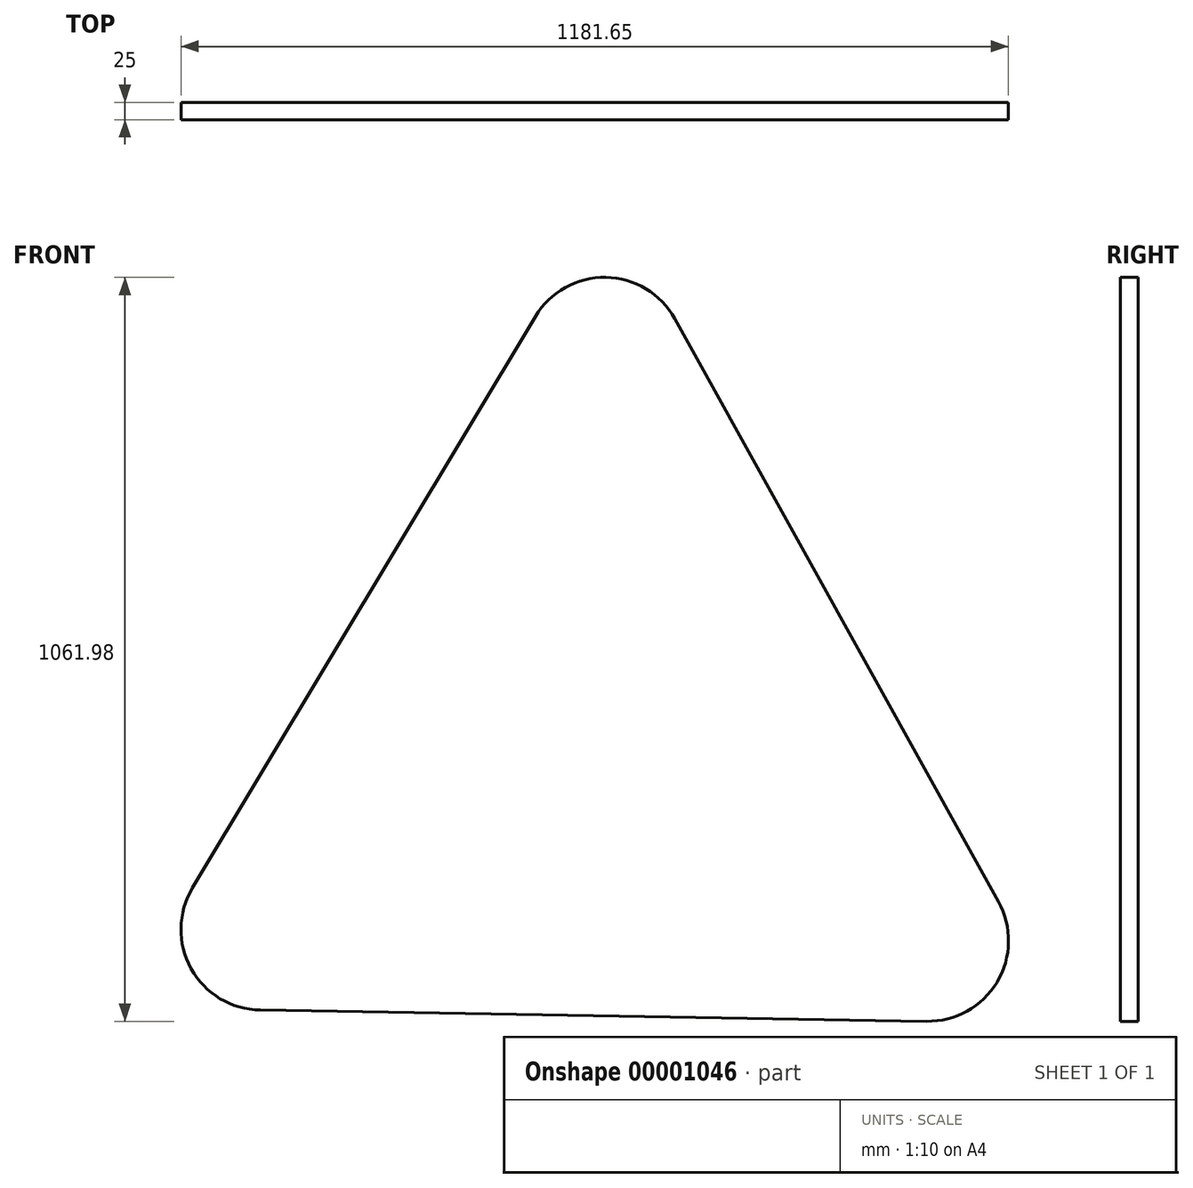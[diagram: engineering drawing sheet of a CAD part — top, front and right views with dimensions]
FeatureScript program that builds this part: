
annotation { "Feature Type Name" : "Feature", "Feature Type Description" : "" }
export const myFeature = defineFeature(function(context is Context, id is Id, definition is map)
    precondition{}
    {
        {
            var Q0;
            Q0=qCreatedBy(makeId("Front.planeOp"),FACE);
            var sketch = newSketch(context, id + "F0", { "sketchPlane" : qUnion([Q0])});
            skLineSegment(sketch, "E0", {"start": v(-635.9, -424.63) * mm, "end": v(-146.24, 391.38) * mm});
            skLineSegment(sketch, "E1", {"start": v(52.9, 388.04) * mm, "end": v(514.9, -443.94) * mm});
            skLineSegment(sketch, "E2", {"start": v(412.43, -614.75) * mm, "end": v(-539.22, -598.78) * mm});
            skPoint(sketch, "E3.visualSharp", {"position": v(-43.78, 562.15) * mm});
            skArc(sketch, "E3.filletArc", {"start": v(52.9, 388.04) * mm, "mid": v(-45.7, 447.2) * mm, "end": v(-146.24, 391.38) * mm});
            skPoint(sketch, "E4.visualSharp", {"position": v(-738.4, -595.44) * mm});
            skArc(sketch, "E4.filletArc", {"start": v(-635.9, -424.63) * mm, "mid": v(-637.83, -539.62) * mm, "end": v(-539.22, -598.78) * mm});
            skPoint(sketch, "E5.visualSharp", {"position": v(611.6, -618.1) * mm});
            skArc(sketch, "E5.filletArc", {"start": v(412.43, -614.75) * mm, "mid": v(512.98, -558.93) * mm, "end": v(514.9, -443.94) * mm});
            skSolve(sketch);
        }
        {
            var Q0;
            Q0=makeQuery(id+"F0.imprint","IMPRINT",FACE,{"disambiguationData":[TD([[makeQuery(id+"F0.imprint","IMPRINT",EDGE,{"derivedFrom":sQuery(id+"F0.wireOp",EDGE,"E0")}),-1.0]])]});
            var sketch = newSketch(context, id + "F1", { "sketchPlane" : qUnion([Q0])});
            skCircle(sketch, "E6", {"center": v(-37.19, -194.42) * mm, "radius": 292.5 * mm});
            skSolve(sketch);
        }
        {
            var Q0;
            Q0=sQuery(id+"F0.wireOp",EDGE,"E0");
            var Q1;
            Q1=sQuery(id+"F0.wireOp",EDGE,"E3.filletArc");
            var Q2;
            Q2=sQuery(id+"F0.wireOp",EDGE,"E1");
            var Q3;
            Q3=sQuery(id+"F0.wireOp",EDGE,"E5.filletArc");
            var Q4;
            Q4=sQuery(id+"F0.wireOp",EDGE,"E2");
            var Q5;
            Q5=sQuery(id+"F0.wireOp",EDGE,"E4.filletArc");
            extrude(context, id + "F2", {"bodyType" : ToolBodyType.SURFACE, "surfaceEntities" : qUnion([Q0, Q1, Q2, Q3, Q4, Q5]), "depth" : 25 * mm});
        }
        {
            var Q0;
            Q0=makeQuery(id+"F0.imprint","IMPRINT",FACE,{"disambiguationData":[TD([[makeQuery(id+"F0.imprint","IMPRINT",EDGE,{"derivedFrom":sQuery(id+"F0.wireOp",EDGE,"E0")}),-1.0]])]});
            extrude(context, id + "F3", {"entities" : qUnion([Q0]), "depth" : 25 * mm});
        }
        {
            var Q0;
            Q0 = qSketchRegion(id + "F1", true);
            extrude(context, id + "F4", {"entities" : qUnion([Q0]), "operationType" : NewBodyOperationType.ADD, "endBound" : BoundingType.UP_TO_NEXT, "depth" : 25 * mm});
        }
    });
